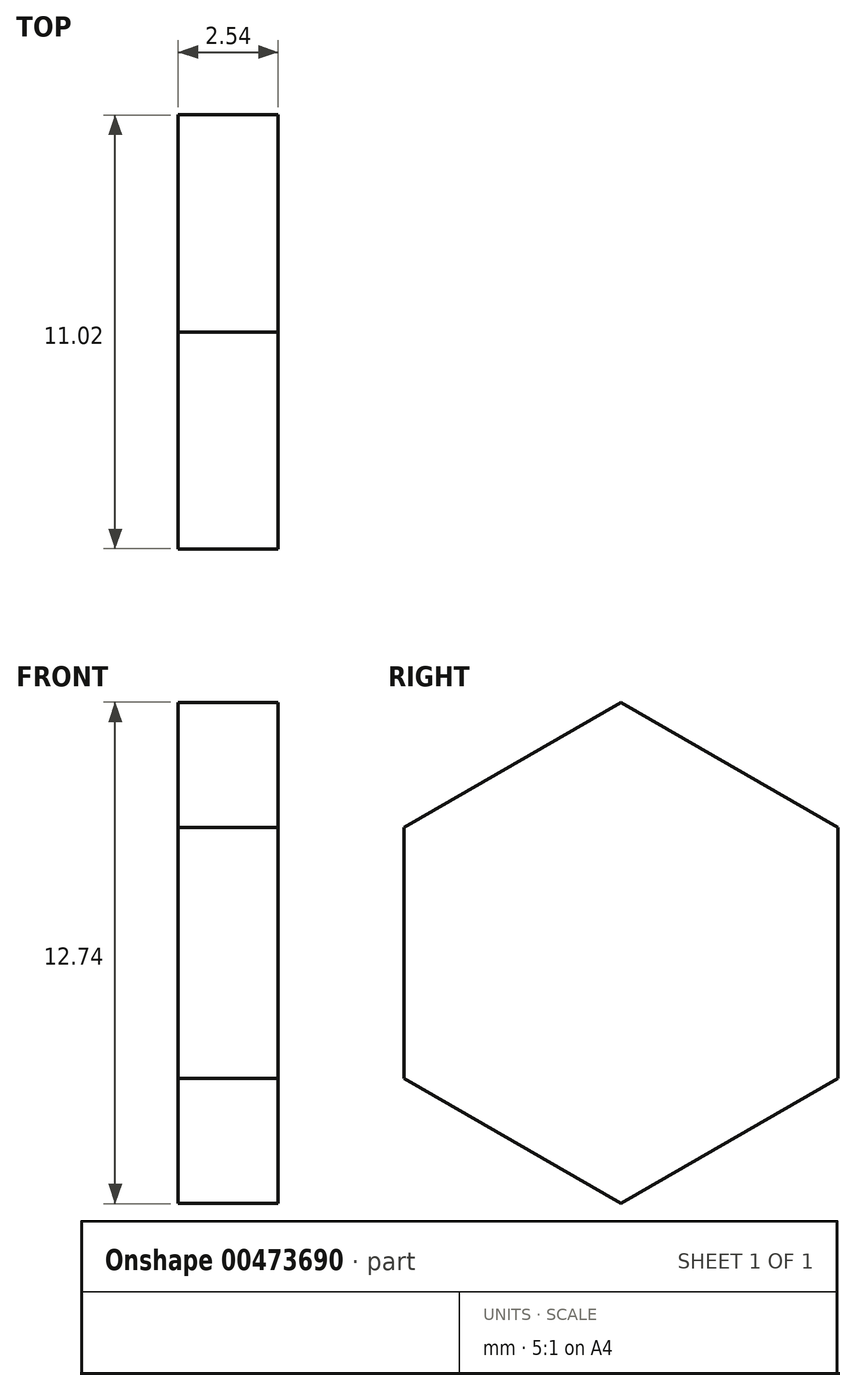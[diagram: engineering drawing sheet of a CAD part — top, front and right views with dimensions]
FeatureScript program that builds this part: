
annotation { "Feature Type Name" : "Feature", "Feature Type Description" : "" }
export const myFeature = defineFeature(function(context is Context, id is Id, definition is map)
    precondition{}
    {
        {
            var Q0;
            Q0=qCreatedBy(makeId("Right.planeOp"),FACE);
            var sketch = newSketch(context, id + "F0", { "sketchPlane" : qUnion([Q0])});
            skCircle(sketch, "E0.cCircle", {"center": v(0, 0) * mm, "radius": 5.51 * mm, "construction": true});
            skLineSegment(sketch, "E0.0", {"start": v(5.51, 3.18) * mm, "end": v(5.51, -3.18) * mm});
            skLineSegment(sketch, "E0.1", {"start": v(5.51, -3.18) * mm, "end": v(0, -6.37) * mm});
            skLineSegment(sketch, "E0.2", {"start": v(0, -6.37) * mm, "end": v(-5.51, -3.18) * mm});
            skLineSegment(sketch, "E0.3", {"start": v(-5.51, -3.18) * mm, "end": v(-5.51, 3.18) * mm});
            skLineSegment(sketch, "E0.4", {"start": v(-5.51, 3.18) * mm, "end": v(0, 6.37) * mm});
            skLineSegment(sketch, "E0.5", {"start": v(0, 6.37) * mm, "end": v(5.51, 3.18) * mm});
            skPoint(sketch, "E0.0.midPoint", {"position": v(5.51, 0) * mm});
            skSolve(sketch);
        }
        {
            var Q0;
            Q0=makeQuery(id+"F0.imprint","IMPRINT",FACE,{"disambiguationData":[TD([[makeQuery(id+"F0.imprint","IMPRINT",EDGE,{"derivedFrom":sQuery(id+"F0.wireOp",EDGE,"E0.0")}),-1.0]])]});
            extrude(context, id + "F1", {"entities" : qUnion([Q0]), "depth" : 2.54 * mm});
        }
    });
